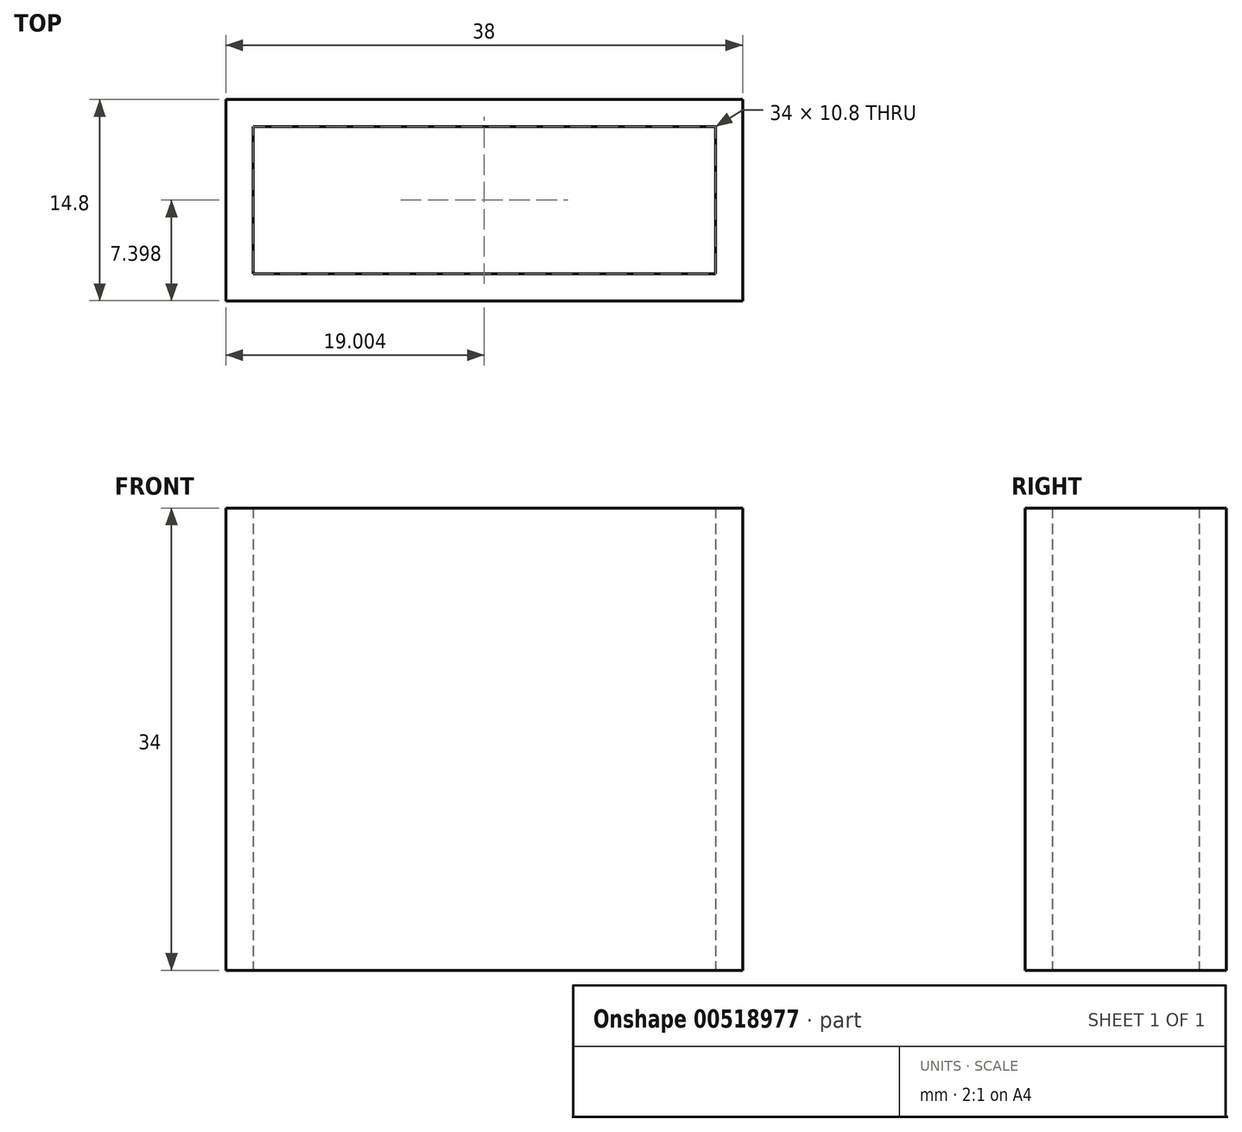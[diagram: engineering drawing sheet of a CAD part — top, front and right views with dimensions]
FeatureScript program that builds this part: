
annotation { "Feature Type Name" : "Feature", "Feature Type Description" : "" }
export const myFeature = defineFeature(function(context is Context, id is Id, definition is map)
    precondition{}
    {
        {
            var Q0;
            Q0=qCreatedBy(makeId("Top.planeOp"),FACE);
            var sketch = newSketch(context, id + "F0", { "sketchPlane" : qUnion([Q0])});
            skLineSegment(sketch, "E0.bottom", {"start": v(-18.9, 3.1) * mm, "end": v(15.1, 3.1) * mm});
            skLineSegment(sketch, "E0.top", {"start": v(-18.9, -7.7) * mm, "end": v(15.1, -7.7) * mm});
            skLineSegment(sketch, "E0.left", {"start": v(-18.9, 3.1) * mm, "end": v(-18.9, -7.7) * mm});
            skLineSegment(sketch, "E0.right", {"start": v(15.1, 3.1) * mm, "end": v(15.1, -7.7) * mm});
            skLineSegment(sketch, "E1.bottom", {"start": v(-20.9, 5.1) * mm, "end": v(17.1, 5.1) * mm});
            skLineSegment(sketch, "E1.top", {"start": v(-20.9, -9.7) * mm, "end": v(17.1, -9.7) * mm});
            skLineSegment(sketch, "E1.left", {"start": v(-20.9, 5.1) * mm, "end": v(-20.9, -9.7) * mm});
            skLineSegment(sketch, "E1.right", {"start": v(17.1, 5.1) * mm, "end": v(17.1, -9.7) * mm});
            skSolve(sketch);
        }
        {
            var Q0;
            Q0=makeQuery(id+"F0.imprint","IMPRINT",FACE,{"disambiguationData":[TD([[makeQuery(id+"F0.imprint","IMPRINT",EDGE,{"derivedFrom":sQuery(id+"F0.wireOp",EDGE,"E0.bottom")}),1.0]])]});
            extrude(context, id + "F1", {"entities" : qUnion([Q0]), "depth" : 34 * mm, "offsetDistance" : 25 * mm});
        }
    });
